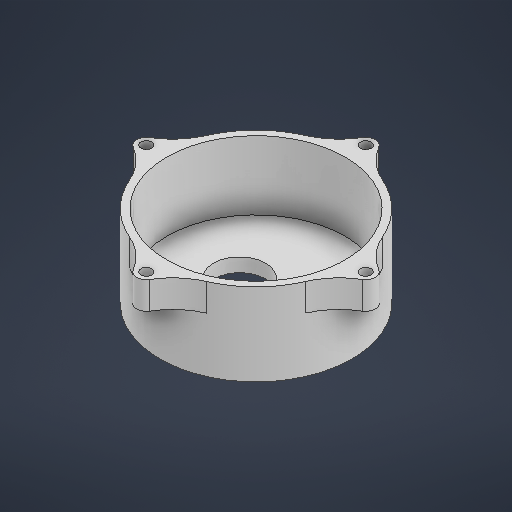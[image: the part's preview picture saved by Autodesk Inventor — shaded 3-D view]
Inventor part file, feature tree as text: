
AUTODESK INVENTOR PART (.ipt)
format: ipt  version: 2025.3 (Build 293356000, 356)  size: 258,560 bytes
history: native  units: mm
features: sketch x4, extrude x4, plane x2
ambient origin geometry x8: Origin, YZ Plane, XZ Plane, XY Plane, X Axis, Y Axis, Z Axis, Center Point
bodies: Body1 (feature_tree)
feature tree (10):
  sketch  "Sketch1"  dims[d0=70.0mm d2=65.0mm]
  extrude  "Extrusion3"  Depth=65.0mm
  extrude  "Extrusion4"  Depth=30.0mm TaperAngle=0.0deg
  plane  "Work Plane1"
  plane  "Work Plane2"
  extrude  "Extrusion9"  Depth=4.0mm
  extrude  "Extrusion10"  Depth=24.0mm
  sketch  "Sketch5"  dims[d19=17.5mm d24=-40.0mm d37=4.0mm]
  sketch  "Sketch Circular Pattern1"  dims[d7=5.0mm d8=0.0mm d9=30.0mm d10=0.0mm]
  sketch  "Sketch6"  dims[d38=7.0mm d40=24.0mm d41=40.0mm d42=40.0mm d44=360.0deg d46=10.0mm d47=0.0mm d48=19.0mm d49=6.0mm d50=10.0mm d51=0.0mm d25=0.872665mm d26=0.5mm d27=0.872665mm d29=0.5mm d30=0.872665mm d31=0.5mm d32=0.872665mm]
